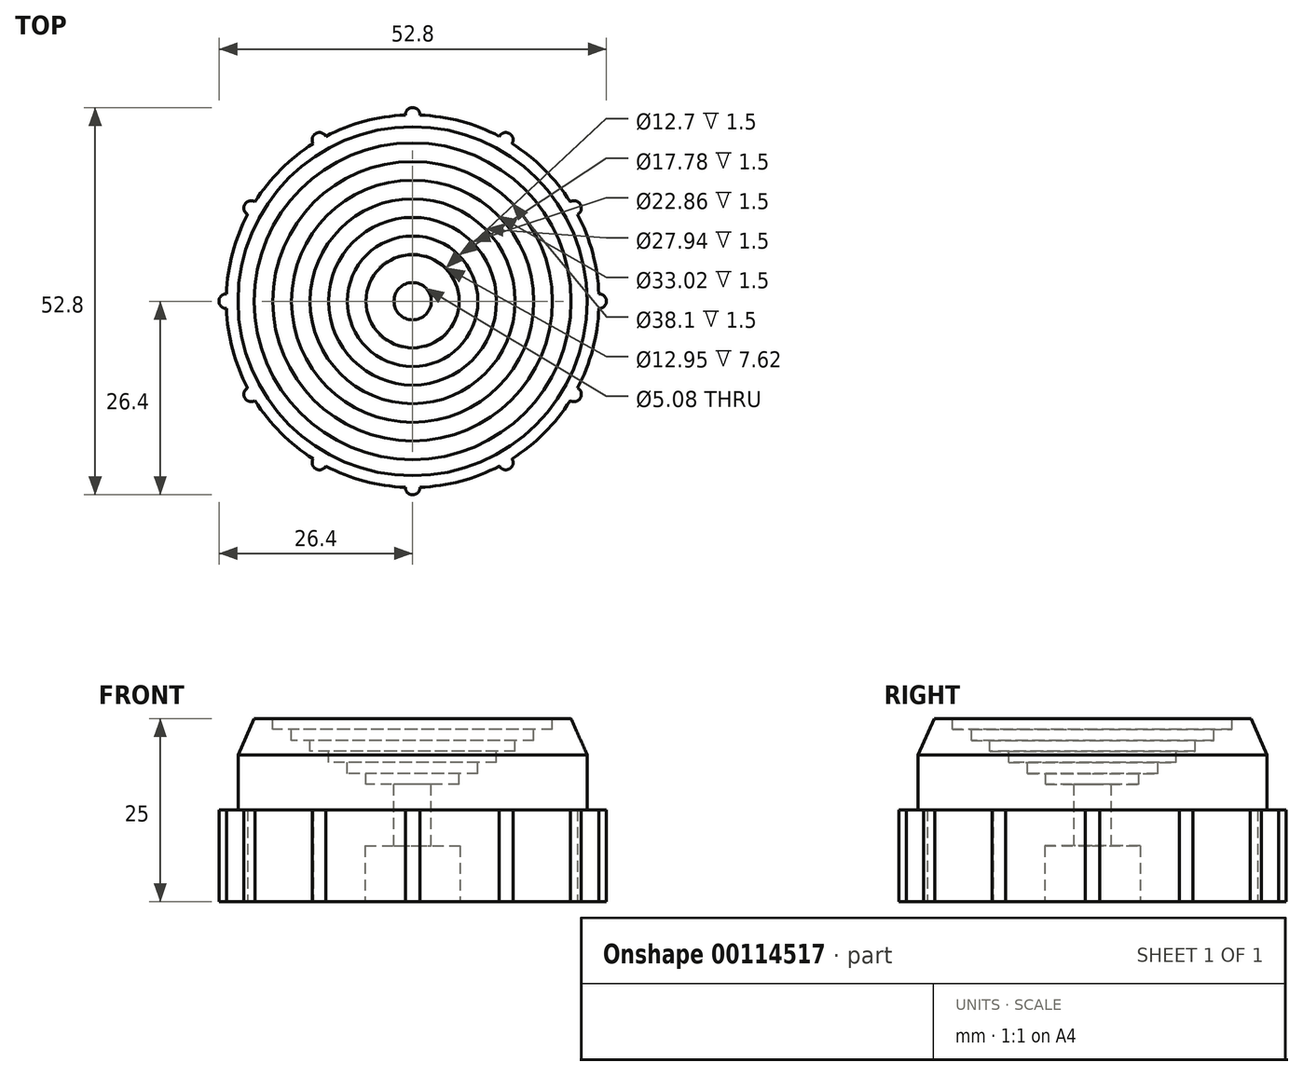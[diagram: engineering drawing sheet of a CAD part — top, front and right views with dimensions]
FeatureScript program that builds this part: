
annotation { "Feature Type Name" : "Feature", "Feature Type Description" : "" }
export const myFeature = defineFeature(function(context is Context, id is Id, definition is map)
    precondition{}
    {
        {
            var Q0;
            Q0=qCreatedBy(makeId("Front.planeOp"),FACE);
            var sketch = newSketch(context, id + "F0", { "sketchPlane" : qUnion([Q0])});
            skLineSegment(sketch, "E0", {"start": v(0, 0) * mm, "end": v(-25.4, 0) * mm});
            skLineSegment(sketch, "E1", {"start": v(-25.4, 0) * mm, "end": v(-25.4, 12.5) * mm});
            skLineSegment(sketch, "E2", {"start": v(-25.4, 12.5) * mm, "end": v(-23.8, 12.5) * mm});
            skLineSegment(sketch, "E3", {"start": v(-23.8, 12.5) * mm, "end": v(-23.8, 20) * mm});
            skLineSegment(sketch, "E4", {"start": v(-23.8, 20) * mm, "end": v(-21.6, 25) * mm});
            skLineSegment(sketch, "E5", {"start": v(-21.6, 25) * mm, "end": v(-19.05, 25) * mm});
            skLineSegment(sketch, "E6", {"start": v(-19.05, 25) * mm, "end": v(-19.05, 23.5) * mm});
            skLineSegment(sketch, "E7", {"start": v(-19.05, 23.5) * mm, "end": v(-16.51, 23.5) * mm});
            skLineSegment(sketch, "E8", {"start": v(-16.51, 23.5) * mm, "end": v(-16.51, 22) * mm});
            skLineSegment(sketch, "E9", {"start": v(-16.51, 22) * mm, "end": v(-13.97, 22) * mm});
            skLineSegment(sketch, "E10", {"start": v(-13.97, 22) * mm, "end": v(-13.97, 20.5) * mm});
            skLineSegment(sketch, "E11", {"start": v(-13.97, 20.5) * mm, "end": v(-11.43, 20.5) * mm});
            skLineSegment(sketch, "E12", {"start": v(-11.43, 20.5) * mm, "end": v(-11.43, 19) * mm});
            skLineSegment(sketch, "E13", {"start": v(-11.43, 19) * mm, "end": v(-8.9, 19) * mm});
            skLineSegment(sketch, "E14", {"start": v(-8.9, 19) * mm, "end": v(-8.9, 17.5) * mm});
            skLineSegment(sketch, "E15", {"start": v(-8.9, 17.5) * mm, "end": v(-6.35, 17.5) * mm});
            skLineSegment(sketch, "E16", {"start": v(-6.35, 17.5) * mm, "end": v(-6.35, 16) * mm});
            skLineSegment(sketch, "E17", {"start": v(-6.35, 16) * mm, "end": v(0, 16) * mm});
            skLineSegment(sketch, "E18", {"start": v(0, 16) * mm, "end": v(0, 0) * mm});
            skLineSegment(sketch, "E19", {"start": v(-23.8, 12.5) * mm, "end": v(0, 12.5) * mm, "construction": true});
            skLineSegment(sketch, "E20", {"start": v(-21.6, 25) * mm, "end": v(-21.6, 12.5) * mm, "construction": true});
            skSolve(sketch);
        }
        {
            var Q0;
            Q0=makeQuery(id+"F0.imprint","IMPRINT",FACE,{"disambiguationData":[TD([[makeQuery(id+"F0.imprint","IMPRINT",EDGE,{"derivedFrom":sQuery(id+"F0.wireOp",EDGE,"E0")}),-1.0]])]});
            var Q1;
            Q1=sQuery(id+"F0.wireOp",EDGE,"E18");
            revolve(context, id + "F1", {"entities" : qUnion([Q0]), "axis" : qUnion([Q1]), "revolveType" : RevolveType.FULL});
        }
        {
            var Q0;
            Q0=makeQuery(id+"F1.opRevolve","SWEPT_FACE",FACE,{"disambiguationData":[OSD([sQuery(id+"F0.wireOp",EDGE,"E0")])]});
            var sketch = newSketch(context, id + "F2", { "sketchPlane" : qUnion([Q0])});
            skCircle(sketch, "E21", {"center": v(0, 0) * mm, "radius": 6.48 * mm});
            skCircle(sketch, "E22", {"center": v(-25.4, 0) * mm, "radius": 1 * mm});
            skCircle(sketch, "E23.1.0", {"center": v(-22, -12.7) * mm, "radius": 1 * mm});
            skCircle(sketch, "E23.2.0", {"center": v(-12.7, -22) * mm, "radius": 1 * mm});
            skCircle(sketch, "E23.3.0", {"center": v(0, -25.4) * mm, "radius": 1 * mm});
            skCircle(sketch, "E23.4.0", {"center": v(12.7, -22) * mm, "radius": 1 * mm});
            skCircle(sketch, "E23.5.0", {"center": v(22, -12.7) * mm, "radius": 1 * mm});
            skCircle(sketch, "E23.6.0", {"center": v(25.4, 0) * mm, "radius": 1 * mm});
            skCircle(sketch, "E23.7.0", {"center": v(22, 12.7) * mm, "radius": 1 * mm});
            skCircle(sketch, "E23.8.0", {"center": v(12.7, 22) * mm, "radius": 1 * mm});
            skCircle(sketch, "E23.9.0", {"center": v(0, 25.4) * mm, "radius": 1 * mm});
            skCircle(sketch, "E23.10.0", {"center": v(-12.7, 22) * mm, "radius": 1 * mm});
            skCircle(sketch, "E23.11.0", {"center": v(-22, 12.7) * mm, "radius": 1 * mm});
            skSolve(sketch);
        }
        {
            var Q0;
            {var subQ0=sQuery(id+"F2.wireOp",EDGE,"E22");var subQ1=makeQuery(id+"F1.opRevolve","SWEPT_EDGE",EDGE,{"disambiguationData":[OSD([sQuery(id+"F0.wireOp",EDGE,"E0"),sQuery(id+"F0.wireOp",EDGE,"E1")])]});var subQ2=makeQuery(id+"F2.imprint","INTERSECT",VERTEX,{"disambiguationData":[OD(0.0)],"derivedFrom":[subQ1,subQ0]});Q0=makeQuery(id+"F2.imprint","IMPRINT",FACE,{"disambiguationData":[TD([[makeQuery(id+"F2.imprint","IMPRINT",EDGE,{"disambiguationData":[TD([[subQ2,-1.0]])],"derivedFrom":subQ0}),1.0]])]});}
            var Q1;
            {var subQ0=sQuery(id+"F2.wireOp",EDGE,"E23.11.0");var subQ1=makeQuery(id+"F1.opRevolve","SWEPT_EDGE",EDGE,{"disambiguationData":[OSD([sQuery(id+"F0.wireOp",EDGE,"E0"),sQuery(id+"F0.wireOp",EDGE,"E1")])]});var subQ2=makeQuery(id+"F2.imprint","INTERSECT",VERTEX,{"disambiguationData":[OD(0.0)],"derivedFrom":[subQ1,subQ0]});Q1=makeQuery(id+"F2.imprint","IMPRINT",FACE,{"disambiguationData":[TD([[makeQuery(id+"F2.imprint","IMPRINT",EDGE,{"disambiguationData":[TD([[subQ2,1.0]])],"derivedFrom":subQ0}),1.0]])]});}
            var Q2;
            {var subQ0=sQuery(id+"F2.wireOp",EDGE,"E23.10.0");var subQ1=makeQuery(id+"F1.opRevolve","SWEPT_EDGE",EDGE,{"disambiguationData":[OSD([sQuery(id+"F0.wireOp",EDGE,"E0"),sQuery(id+"F0.wireOp",EDGE,"E1")])]});var subQ2=makeQuery(id+"F2.imprint","INTERSECT",VERTEX,{"disambiguationData":[OD(0.0)],"derivedFrom":[subQ1,subQ0]});Q2=makeQuery(id+"F2.imprint","IMPRINT",FACE,{"disambiguationData":[TD([[makeQuery(id+"F2.imprint","IMPRINT",EDGE,{"disambiguationData":[TD([[subQ2,1.0]])],"derivedFrom":subQ0}),1.0]])]});}
            var Q3;
            {var subQ0=sQuery(id+"F2.wireOp",EDGE,"E23.9.0");var subQ1=makeQuery(id+"F1.opRevolve","SWEPT_EDGE",EDGE,{"disambiguationData":[OSD([sQuery(id+"F0.wireOp",EDGE,"E0"),sQuery(id+"F0.wireOp",EDGE,"E1")])]});var subQ2=makeQuery(id+"F2.imprint","INTERSECT",VERTEX,{"disambiguationData":[OD(0.0)],"derivedFrom":[subQ1,subQ0]});Q3=makeQuery(id+"F2.imprint","IMPRINT",FACE,{"disambiguationData":[TD([[makeQuery(id+"F2.imprint","IMPRINT",EDGE,{"disambiguationData":[TD([[subQ2,1.0]])],"derivedFrom":subQ0}),1.0]])]});}
            var Q4;
            {var subQ0=sQuery(id+"F2.wireOp",EDGE,"E23.8.0");var subQ1=makeQuery(id+"F1.opRevolve","SWEPT_EDGE",EDGE,{"disambiguationData":[OSD([sQuery(id+"F0.wireOp",EDGE,"E0"),sQuery(id+"F0.wireOp",EDGE,"E1")])]});var subQ2=makeQuery(id+"F2.imprint","INTERSECT",VERTEX,{"disambiguationData":[OD(0.0)],"derivedFrom":[subQ1,subQ0]});Q4=makeQuery(id+"F2.imprint","IMPRINT",FACE,{"disambiguationData":[TD([[makeQuery(id+"F2.imprint","IMPRINT",EDGE,{"disambiguationData":[TD([[subQ2,1.0]])],"derivedFrom":subQ0}),1.0]])]});}
            var Q5;
            {var subQ0=sQuery(id+"F2.wireOp",EDGE,"E23.7.0");var subQ1=makeQuery(id+"F1.opRevolve","SWEPT_EDGE",EDGE,{"disambiguationData":[OSD([sQuery(id+"F0.wireOp",EDGE,"E0"),sQuery(id+"F0.wireOp",EDGE,"E1")])]});var subQ2=makeQuery(id+"F2.imprint","INTERSECT",VERTEX,{"disambiguationData":[OD(0.0)],"derivedFrom":[subQ1,subQ0]});Q5=makeQuery(id+"F2.imprint","IMPRINT",FACE,{"disambiguationData":[TD([[makeQuery(id+"F2.imprint","IMPRINT",EDGE,{"disambiguationData":[TD([[subQ2,1.0]])],"derivedFrom":subQ0}),1.0]])]});}
            var Q6;
            {var subQ0=sQuery(id+"F2.wireOp",EDGE,"E23.6.0");var subQ1=makeQuery(id+"F1.opRevolve","SWEPT_EDGE",EDGE,{"disambiguationData":[OSD([sQuery(id+"F0.wireOp",EDGE,"E0"),sQuery(id+"F0.wireOp",EDGE,"E1")])]});var subQ2=makeQuery(id+"F2.imprint","INTERSECT",VERTEX,{"disambiguationData":[OD(0.0)],"derivedFrom":[subQ1,subQ0]});Q6=makeQuery(id+"F2.imprint","IMPRINT",FACE,{"disambiguationData":[TD([[makeQuery(id+"F2.imprint","IMPRINT",EDGE,{"disambiguationData":[TD([[subQ2,1.0]])],"derivedFrom":subQ0}),1.0]])]});}
            var Q7;
            {var subQ0=sQuery(id+"F2.wireOp",EDGE,"E23.5.0");var subQ1=makeQuery(id+"F1.opRevolve","SWEPT_EDGE",EDGE,{"disambiguationData":[OSD([sQuery(id+"F0.wireOp",EDGE,"E0"),sQuery(id+"F0.wireOp",EDGE,"E1")])]});var subQ2=makeQuery(id+"F2.imprint","INTERSECT",VERTEX,{"disambiguationData":[OD(0.0)],"derivedFrom":[subQ1,subQ0]});Q7=makeQuery(id+"F2.imprint","IMPRINT",FACE,{"disambiguationData":[TD([[makeQuery(id+"F2.imprint","IMPRINT",EDGE,{"disambiguationData":[TD([[subQ2,-1.0]])],"derivedFrom":subQ0}),1.0]])]});}
            var Q8;
            {var subQ0=sQuery(id+"F2.wireOp",EDGE,"E23.4.0");var subQ1=makeQuery(id+"F1.opRevolve","SWEPT_EDGE",EDGE,{"disambiguationData":[OSD([sQuery(id+"F0.wireOp",EDGE,"E0"),sQuery(id+"F0.wireOp",EDGE,"E1")])]});var subQ2=makeQuery(id+"F2.imprint","INTERSECT",VERTEX,{"disambiguationData":[OD(0.0)],"derivedFrom":[subQ1,subQ0]});Q8=makeQuery(id+"F2.imprint","IMPRINT",FACE,{"disambiguationData":[TD([[makeQuery(id+"F2.imprint","IMPRINT",EDGE,{"disambiguationData":[TD([[subQ2,-1.0]])],"derivedFrom":subQ0}),1.0]])]});}
            var Q9;
            {var subQ0=sQuery(id+"F2.wireOp",EDGE,"E23.3.0");var subQ1=makeQuery(id+"F1.opRevolve","SWEPT_EDGE",EDGE,{"disambiguationData":[OSD([sQuery(id+"F0.wireOp",EDGE,"E0"),sQuery(id+"F0.wireOp",EDGE,"E1")])]});var subQ2=makeQuery(id+"F2.imprint","INTERSECT",VERTEX,{"disambiguationData":[OD(0.0)],"derivedFrom":[subQ1,subQ0]});Q9=makeQuery(id+"F2.imprint","IMPRINT",FACE,{"disambiguationData":[TD([[makeQuery(id+"F2.imprint","IMPRINT",EDGE,{"disambiguationData":[TD([[subQ2,-1.0]])],"derivedFrom":subQ0}),1.0]])]});}
            var Q10;
            {var subQ0=sQuery(id+"F2.wireOp",EDGE,"E23.2.0");var subQ1=makeQuery(id+"F1.opRevolve","SWEPT_EDGE",EDGE,{"disambiguationData":[OSD([sQuery(id+"F0.wireOp",EDGE,"E0"),sQuery(id+"F0.wireOp",EDGE,"E1")])]});var subQ2=makeQuery(id+"F2.imprint","INTERSECT",VERTEX,{"disambiguationData":[OD(0.0)],"derivedFrom":[subQ1,subQ0]});Q10=makeQuery(id+"F2.imprint","IMPRINT",FACE,{"disambiguationData":[TD([[makeQuery(id+"F2.imprint","IMPRINT",EDGE,{"disambiguationData":[TD([[subQ2,-1.0]])],"derivedFrom":subQ0}),1.0]])]});}
            var Q11;
            {var subQ0=sQuery(id+"F2.wireOp",EDGE,"E23.1.0");var subQ1=makeQuery(id+"F1.opRevolve","SWEPT_EDGE",EDGE,{"disambiguationData":[OSD([sQuery(id+"F0.wireOp",EDGE,"E0"),sQuery(id+"F0.wireOp",EDGE,"E1")])]});var subQ2=makeQuery(id+"F2.imprint","INTERSECT",VERTEX,{"disambiguationData":[OD(0.0)],"derivedFrom":[subQ1,subQ0]});Q11=makeQuery(id+"F2.imprint","IMPRINT",FACE,{"disambiguationData":[TD([[makeQuery(id+"F2.imprint","IMPRINT",EDGE,{"disambiguationData":[TD([[subQ2,-1.0]])],"derivedFrom":subQ0}),1.0]])]});}
            extrude(context, id + "F3", {"entities" : qUnion([Q0, Q1, Q2, Q3, Q4, Q5, Q6, Q7, Q8, Q9, Q10, Q11]), "operationType" : NewBodyOperationType.ADD, "oppositeDirection" : true, "depth" : 12.5 * mm});
        }
        {
            var Q0;
            Q0=makeQuery(id+"F2.imprint","IMPRINT",FACE,{"disambiguationData":[TD([[makeQuery(id+"F2.imprint","IMPRINT",EDGE,{"derivedFrom":sQuery(id+"F2.wireOp",EDGE,"E21")}),1.0]])]});
            extrude(context, id + "F4", {"entities" : qUnion([Q0]), "operationType" : NewBodyOperationType.REMOVE, "oppositeDirection" : true, "depth" : 7.62 * mm});
        }
        {
            var Q0;
            Q0=makeQuery(id+"F1.opRevolve","SWEPT_FACE",FACE,{"disambiguationData":[OSD([sQuery(id+"F0.wireOp",EDGE,"E17")])]});
            var sketch = newSketch(context, id + "F5", { "sketchPlane" : qUnion([Q0])});
            skCircle(sketch, "E24", {"center": v(0, 0) * mm, "radius": 2.54 * mm});
            skSolve(sketch);
        }
        {
            var Q0;
            Q0=makeQuery(id+"F5.imprint","IMPRINT",FACE,{"disambiguationData":[TD([[makeQuery(id+"F5.imprint","IMPRINT",EDGE,{"derivedFrom":sQuery(id+"F5.wireOp",EDGE,"E24")}),1.0]])]});
            extrude(context, id + "F6", {"entities" : qUnion([Q0]), "operationType" : NewBodyOperationType.REMOVE, "oppositeDirection" : true, "depth" : 25.4 * mm});
        }
    });
